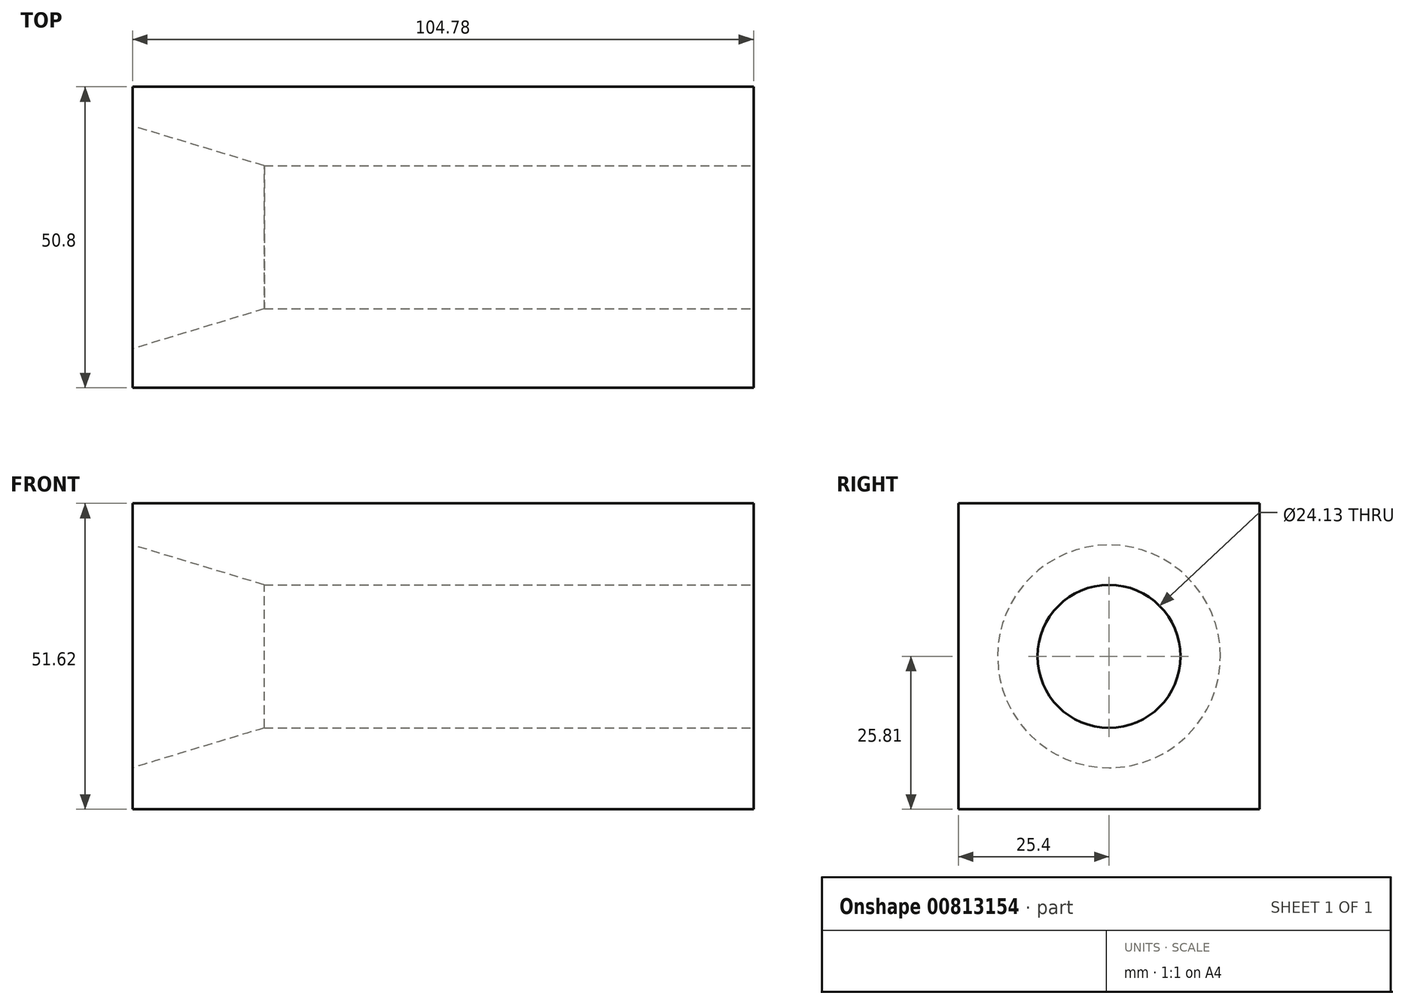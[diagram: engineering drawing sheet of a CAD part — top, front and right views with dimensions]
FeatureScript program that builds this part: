
annotation { "Feature Type Name" : "Feature", "Feature Type Description" : "" }
export const myFeature = defineFeature(function(context is Context, id is Id, definition is map)
    precondition{}
    {
        {
            var Q0;
            Q0=qCreatedBy(makeId("Front.planeOp"),FACE);
            var sketch = newSketch(context, id + "F0", { "sketchPlane" : qUnion([Q0])});
            skLineSegment(sketch, "E0", {"start": v(-58.64, 0) * mm, "end": v(57.38, 0) * mm, "construction": true});
            skLineSegment(sketch, "E1", {"start": v(47.43, 0) * mm, "end": v(47.43, 12.06) * mm});
            skLineSegment(sketch, "E2", {"start": v(47.43, 12.07) * mm, "end": v(-35.12, 12.06) * mm});
            skLineSegment(sketch, "E3", {"start": v(-35.12, 12.06) * mm, "end": v(-57.35, 18.8) * mm});
            skLineSegment(sketch, "E4.MirrorCS", {"start": v(-35.12, -12.06) * mm, "end": v(-57.35, -18.8) * mm});
            skLineSegment(sketch, "E5.MirrorCS", {"start": v(47.43, -12.07) * mm, "end": v(-35.12, -12.06) * mm});
            skLineSegment(sketch, "E6.MirrorCS", {"start": v(47.43, 0) * mm, "end": v(47.43, -12.06) * mm});
            skLineSegment(sketch, "E7", {"start": v(-57.35, 18.8) * mm, "end": v(-57.35, -18.8) * mm});
            skLineSegment(sketch, "E8", {"start": v(-57.35, -18.8) * mm, "end": v(-57.35, -25.81) * mm});
            skLineSegment(sketch, "E9", {"start": v(-57.35, -25.81) * mm, "end": v(47.43, -25.81) * mm});
            skLineSegment(sketch, "E10", {"start": v(47.43, -25.81) * mm, "end": v(47.43, -12.06) * mm});
            skLineSegment(sketch, "E11.MirrorCS", {"start": v(-57.35, 18.8) * mm, "end": v(-57.35, 25.81) * mm});
            skLineSegment(sketch, "E12.MirrorCS", {"start": v(-57.35, 25.81) * mm, "end": v(47.43, 25.81) * mm});
            skLineSegment(sketch, "E13.MirrorCS", {"start": v(47.43, 25.81) * mm, "end": v(47.43, 12.06) * mm});
            skLineSegment(sketch, "E14", {"start": v(-58.64, 0) * mm, "end": v(47.43, 0) * mm});
            skSolve(sketch);
        }
        {
            var Q0;
            Q0 = qSketchRegion(id + "F0", true);
            extrude(context, id + "F1", {"entities" : qUnion([Q0]), "endBound" : BoundingType.SYMMETRIC, "depth" : 50.8 * mm, "offsetDistance" : 25.4 * mm});
        }
        {
            var Q0;
            {var subQ4=sQuery(id+"F0.wireOp",EDGE,"E1");Q0=makeQuery(id+"F0.imprint","IMPRINT",FACE,{"disambiguationData":[TD([[makeQuery(id+"F0.imprint","IMPRINT",EDGE,{"derivedFrom":subQ4}),1.0]])]});}
            var Q1;
            Q1=sQuery(id+"F0.wireOp",EDGE,"E14");
            revolve(context, id + "F2", {"operationType" : NewBodyOperationType.REMOVE, "surfaceOperationType" : NewSurfaceOperationType.NEW, "entities" : qUnion([Q0]), "axis" : qUnion([Q1]), "revolveType" : RevolveType.FULL, "oppositeDirection" : true});
        }
    });
